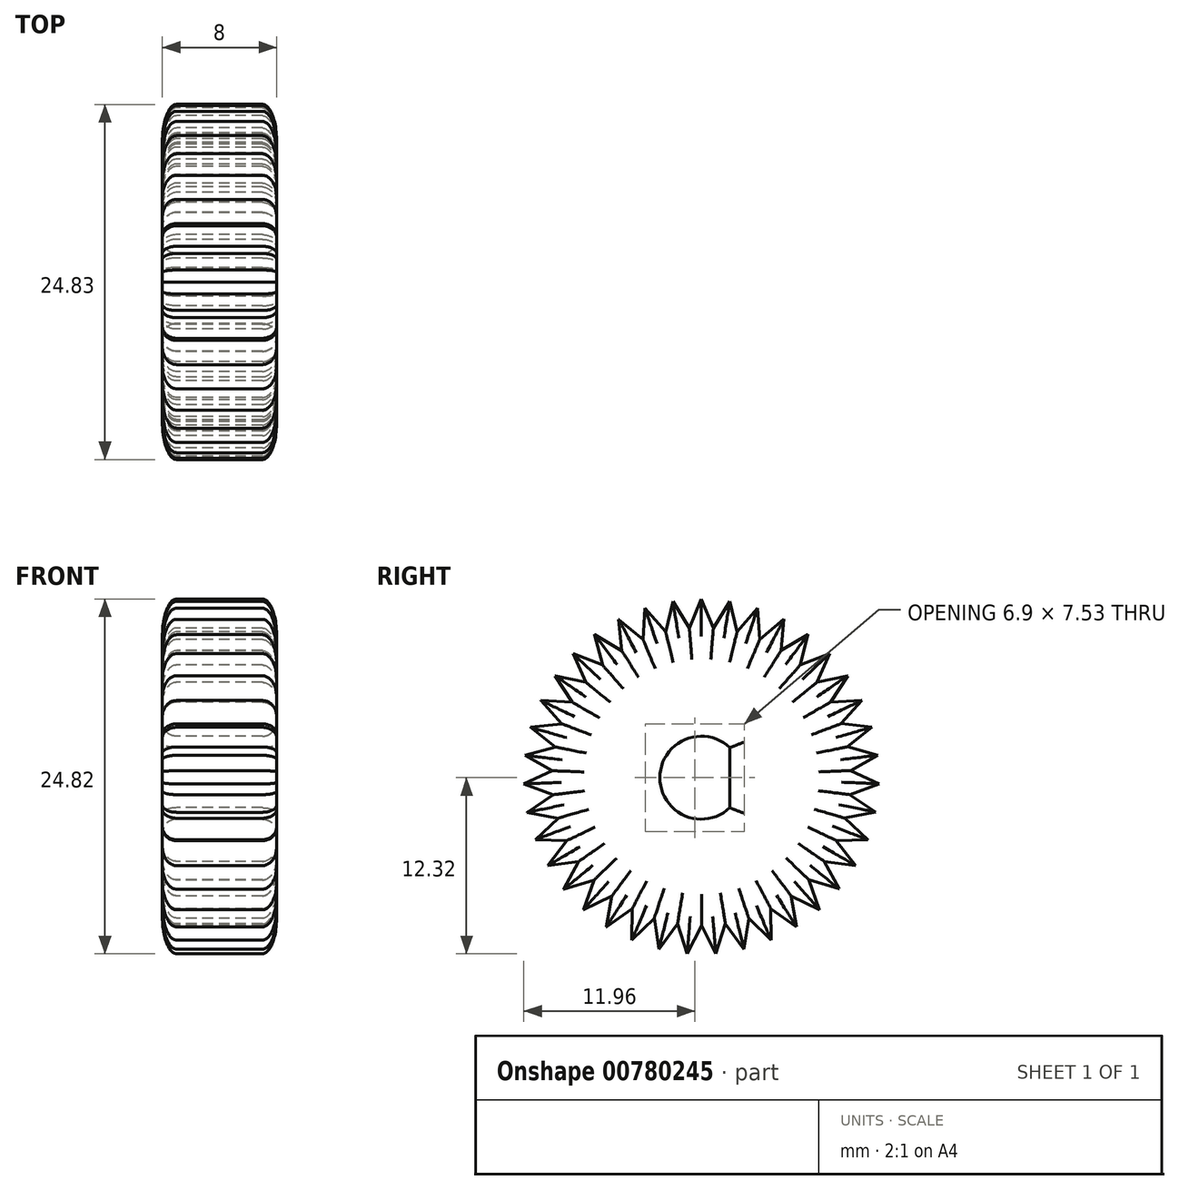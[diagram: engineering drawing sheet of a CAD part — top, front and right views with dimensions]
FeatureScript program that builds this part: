
annotation { "Feature Type Name" : "Feature", "Feature Type Description" : "" }
export const myFeature = defineFeature(function(context is Context, id is Id, definition is map)
    precondition{}
    {
        {
            var Q0;
            Q0=qCreatedBy(makeId("Right.planeOp"),FACE);
            var sketch = newSketch(context, id + "F0", { "sketchPlane" : qUnion([Q0])});
            skCircle(sketch, "E0", {"center": v(0, 0) * mm, "radius": 10.5 * mm, "construction": true});
            skCircle(sketch, "E1", {"center": v(0, 0) * mm, "radius": 2.9 * mm});
            skLineSegment(sketch, "E2", {"start": v(0, 0) * mm, "end": v(0, 12.5) * mm, "construction": true});
            skLineSegment(sketch, "E3", {"start": v(0, 12.5) * mm, "end": v(0.84, 10.47) * mm});
            skCircle(sketch, "E4", {"center": v(0, 0) * mm, "radius": 12.5 * mm, "construction": true});
            skLineSegment(sketch, "E5", {"start": v(0.84, 10.47) * mm, "end": v(2, 12.34) * mm});
            skLineSegment(sketch, "E6", {"start": v(2, 12.34) * mm, "end": v(0, 0) * mm, "construction": true});
            skLineSegment(sketch, "E7.1.0", {"start": v(-2, 12.34) * mm, "end": v(-0.84, 10.47) * mm});
            skLineSegment(sketch, "E7.1.1", {"start": v(-0.84, 10.47) * mm, "end": v(0, 12.5) * mm});
            skLineSegment(sketch, "E7.2.0", {"start": v(-3.94, 11.86) * mm, "end": v(-2.5, 10.2) * mm});
            skLineSegment(sketch, "E7.2.1", {"start": v(-2.5, 10.2) * mm, "end": v(-2, 12.34) * mm});
            skLineSegment(sketch, "E7.3.0", {"start": v(-5.77, 11.07) * mm, "end": v(-4.09, 9.66) * mm});
            skLineSegment(sketch, "E7.3.1", {"start": v(-4.09, 9.66) * mm, "end": v(-3.94, 11.86) * mm});
            skLineSegment(sketch, "E7.4.0", {"start": v(-7.46, 10) * mm, "end": v(-5.57, 8.88) * mm});
            skLineSegment(sketch, "E7.4.1", {"start": v(-5.57, 8.88) * mm, "end": v(-5.77, 11.07) * mm});
            skLineSegment(sketch, "E7.5.0", {"start": v(-8.96, 8.68) * mm, "end": v(-6.91, 7.87) * mm});
            skLineSegment(sketch, "E7.5.1", {"start": v(-6.91, 7.87) * mm, "end": v(-7.46, 10) * mm});
            skLineSegment(sketch, "E7.6.0", {"start": v(-10.23, 7.13) * mm, "end": v(-8.07, 6.66) * mm});
            skLineSegment(sketch, "E7.6.1", {"start": v(-8.07, 6.66) * mm, "end": v(-8.96, 8.68) * mm});
            skLineSegment(sketch, "E7.7.0", {"start": v(-11.22, 5.4) * mm, "end": v(-9.03, 5.28) * mm});
            skLineSegment(sketch, "E7.7.1", {"start": v(-9.03, 5.28) * mm, "end": v(-10.23, 7.13) * mm});
            skLineSegment(sketch, "E7.8.0", {"start": v(-11.93, 3.52) * mm, "end": v(-9.75, 3.77) * mm});
            skLineSegment(sketch, "E7.8.1", {"start": v(-9.75, 3.77) * mm, "end": v(-11.22, 5.4) * mm});
            skLineSegment(sketch, "E7.9.0", {"start": v(-12.33, 1.56) * mm, "end": v(-10.21, 2.15) * mm});
            skLineSegment(sketch, "E7.9.1", {"start": v(-10.21, 2.15) * mm, "end": v(-11.93, 3.52) * mm});
            skLineSegment(sketch, "E7.10.0", {"start": v(-12.41, -0.43) * mm, "end": v(-10.41, 0.49) * mm});
            skLineSegment(sketch, "E7.10.1", {"start": v(-10.41, 0.49) * mm, "end": v(-12.33, 1.56) * mm});
            skLineSegment(sketch, "E7.11.0", {"start": v(-12.17, -2.42) * mm, "end": v(-10.34, -1.19) * mm});
            skLineSegment(sketch, "E7.11.1", {"start": v(-10.34, -1.19) * mm, "end": v(-12.41, -0.43) * mm});
            skLineSegment(sketch, "E7.12.0", {"start": v(-11.61, -4.34) * mm, "end": v(-10, -2.83) * mm});
            skLineSegment(sketch, "E7.12.1", {"start": v(-10, -2.83) * mm, "end": v(-12.17, -2.42) * mm});
            skLineSegment(sketch, "E7.13.0", {"start": v(-10.75, -6.15) * mm, "end": v(-9.41, -4.4) * mm});
            skLineSegment(sketch, "E7.13.1", {"start": v(-9.41, -4.4) * mm, "end": v(-11.61, -4.34) * mm});
            skLineSegment(sketch, "E7.14.0", {"start": v(-9.62, -7.8) * mm, "end": v(-8.57, -5.85) * mm});
            skLineSegment(sketch, "E7.14.1", {"start": v(-8.57, -5.85) * mm, "end": v(-10.75, -6.15) * mm});
            skLineSegment(sketch, "E7.15.0", {"start": v(-8.23, -9.23) * mm, "end": v(-7.51, -7.15) * mm});
            skLineSegment(sketch, "E7.15.1", {"start": v(-7.51, -7.15) * mm, "end": v(-9.62, -7.8) * mm});
            skLineSegment(sketch, "E7.16.0", {"start": v(-6.63, -10.43) * mm, "end": v(-6.25, -8.27) * mm});
            skLineSegment(sketch, "E7.16.1", {"start": v(-6.25, -8.27) * mm, "end": v(-8.23, -9.23) * mm});
            skLineSegment(sketch, "E7.17.0", {"start": v(-4.86, -11.36) * mm, "end": v(-4.84, -9.16) * mm});
            skLineSegment(sketch, "E7.17.1", {"start": v(-4.84, -9.16) * mm, "end": v(-6.63, -10.43) * mm});
            skLineSegment(sketch, "E7.18.0", {"start": v(-2.96, -12) * mm, "end": v(-3.3, -9.82) * mm});
            skLineSegment(sketch, "E7.18.1", {"start": v(-3.3, -9.82) * mm, "end": v(-4.86, -11.36) * mm});
            skLineSegment(sketch, "E7.19.0", {"start": v(-0.99, -12.32) * mm, "end": v(-1.66, -10.22) * mm});
            skLineSegment(sketch, "E7.19.1", {"start": v(-1.66, -10.22) * mm, "end": v(-2.96, -12) * mm});
            skLineSegment(sketch, "E7.20.0", {"start": v(1.01, -12.31) * mm, "end": v(0.01, -10.35) * mm});
            skLineSegment(sketch, "E7.20.1", {"start": v(0.01, -10.35) * mm, "end": v(-0.99, -12.32) * mm});
            skLineSegment(sketch, "E7.21.0", {"start": v(2.99, -12) * mm, "end": v(1.68, -10.22) * mm});
            skLineSegment(sketch, "E7.21.1", {"start": v(1.68, -10.22) * mm, "end": v(1.01, -12.31) * mm});
            skLineSegment(sketch, "E7.22.0", {"start": v(4.88, -11.36) * mm, "end": v(3.31, -9.82) * mm});
            skLineSegment(sketch, "E7.22.1", {"start": v(3.31, -9.82) * mm, "end": v(2.99, -12) * mm});
            skLineSegment(sketch, "E7.23.0", {"start": v(6.65, -10.43) * mm, "end": v(4.86, -9.16) * mm});
            skLineSegment(sketch, "E7.23.1", {"start": v(4.86, -9.16) * mm, "end": v(4.88, -11.36) * mm});
            skLineSegment(sketch, "E7.24.0", {"start": v(8.25, -9.23) * mm, "end": v(6.27, -8.26) * mm});
            skLineSegment(sketch, "E7.24.1", {"start": v(6.27, -8.26) * mm, "end": v(6.65, -10.43) * mm});
            skLineSegment(sketch, "E7.25.0", {"start": v(9.64, -7.78) * mm, "end": v(7.53, -7.15) * mm});
            skLineSegment(sketch, "E7.25.1", {"start": v(7.53, -7.15) * mm, "end": v(8.25, -9.23) * mm});
            skLineSegment(sketch, "E7.26.0", {"start": v(10.77, -6.14) * mm, "end": v(8.6, -5.85) * mm});
            skLineSegment(sketch, "E7.26.1", {"start": v(8.6, -5.85) * mm, "end": v(9.64, -7.78) * mm});
            skLineSegment(sketch, "E7.27.0", {"start": v(11.63, -4.33) * mm, "end": v(9.43, -4.4) * mm});
            skLineSegment(sketch, "E7.27.1", {"start": v(9.43, -4.4) * mm, "end": v(10.77, -6.14) * mm});
            skLineSegment(sketch, "E7.28.0", {"start": v(12.18, -2.4) * mm, "end": v(10.02, -2.82) * mm});
            skLineSegment(sketch, "E7.28.1", {"start": v(10.02, -2.82) * mm, "end": v(11.63, -4.33) * mm});
            skLineSegment(sketch, "E7.29.0", {"start": v(12.42, -0.42) * mm, "end": v(10.36, -1.18) * mm});
            skLineSegment(sketch, "E7.29.1", {"start": v(10.36, -1.18) * mm, "end": v(12.18, -2.4) * mm});
            skLineSegment(sketch, "E7.30.0", {"start": v(12.34, 1.58) * mm, "end": v(10.42, 0.5) * mm});
            skLineSegment(sketch, "E7.30.1", {"start": v(10.42, 0.5) * mm, "end": v(12.42, -0.42) * mm});
            skLineSegment(sketch, "E7.31.0", {"start": v(11.94, 3.54) * mm, "end": v(10.22, 2.16) * mm});
            skLineSegment(sketch, "E7.31.1", {"start": v(10.22, 2.16) * mm, "end": v(12.34, 1.58) * mm});
            skLineSegment(sketch, "E7.32.0", {"start": v(11.23, 5.4) * mm, "end": v(9.75, 3.77) * mm});
            skLineSegment(sketch, "E7.32.1", {"start": v(9.75, 3.77) * mm, "end": v(11.94, 3.54) * mm});
            skLineSegment(sketch, "E7.33.0", {"start": v(10.23, 7.14) * mm, "end": v(9.03, 5.3) * mm});
            skLineSegment(sketch, "E7.33.1", {"start": v(9.03, 5.3) * mm, "end": v(11.23, 5.4) * mm});
            skLineSegment(sketch, "E7.34.0", {"start": v(8.96, 8.69) * mm, "end": v(8.08, 6.67) * mm});
            skLineSegment(sketch, "E7.34.1", {"start": v(8.08, 6.67) * mm, "end": v(10.23, 7.14) * mm});
            skLineSegment(sketch, "E7.35.0", {"start": v(7.47, 10.01) * mm, "end": v(6.92, 7.88) * mm});
            skLineSegment(sketch, "E7.35.1", {"start": v(6.92, 7.88) * mm, "end": v(8.96, 8.69) * mm});
            skLineSegment(sketch, "E7.36.0", {"start": v(5.78, 11.08) * mm, "end": v(5.57, 8.89) * mm});
            skLineSegment(sketch, "E7.36.1", {"start": v(5.57, 8.89) * mm, "end": v(7.47, 10.01) * mm});
            skLineSegment(sketch, "E7.37.0", {"start": v(3.94, 11.86) * mm, "end": v(4.09, 9.67) * mm});
            skLineSegment(sketch, "E7.37.1", {"start": v(4.09, 9.67) * mm, "end": v(5.78, 11.08) * mm});
            skLineSegment(sketch, "E7.38.0", {"start": v(2, 12.34) * mm, "end": v(2.5, 10.2) * mm});
            skLineSegment(sketch, "E7.38.1", {"start": v(2.5, 10.2) * mm, "end": v(3.94, 11.86) * mm});
            skPoint(sketch, "E7.center", {"position": v(0, 0.07) * mm});
            skSolve(sketch);
        }
        {
            var Q0;
            Q0=makeQuery(id+"F0.imprint","IMPRINT",FACE,{"disambiguationData":[TD([[makeQuery(id+"F0.imprint","IMPRINT",EDGE,{"derivedFrom":sQuery(id+"F0.wireOp",EDGE,"E1")}),-1.0]])]});
            extrude(context, id + "F1", {"entities" : qUnion([Q0]), "depth" : 8 * mm, "offsetDistance" : 25.4 * mm});
        }
        {
            var Q0;
            Q0=qCreatedBy(makeId("Right.planeOp"),FACE);
            var sketch = newSketch(context, id + "F2", { "sketchPlane" : qUnion([Q0])});
            skLineSegment(sketch, "E8", {"start": v(2, 2.1) * mm, "end": v(2, -2.1) * mm});
            skArc(sketch, "E9", {"start": v(2, -2.1) * mm, "mid": v(2.9, 0) * mm, "end": v(2, 2.1) * mm});
            skSolve(sketch);
        }
        {
            var Q0;
            Q0=qSketchRegion(id+"F2",true);
            extrude(context, id + "F3", {"entities" : qUnion([Q0]), "operationType" : NewBodyOperationType.ADD, "depth" : 8 * mm, "offsetDistance" : 25.4 * mm});
        }
        {
            var Q0;
            Q0=makeQuery(id+"F3.boolean.opBoolean","MERGE",FACE,{"derivedFrom":[makeQuery(id+"F1.opExtrude","CAP_FACE",FACE,{"disambiguationData":[OSD([sQuery(id+"F0.wireOp",EDGE,"E1"),sQuery(id+"F0.wireOp",EDGE,"E3"),sQuery(id+"F0.wireOp",EDGE,"E5"),sQuery(id+"F0.wireOp",EDGE,"E7.1.0"),sQuery(id+"F0.wireOp",EDGE,"E7.1.1"),sQuery(id+"F0.wireOp",EDGE,"E7.2.0"),sQuery(id+"F0.wireOp",EDGE,"E7.2.1"),sQuery(id+"F0.wireOp",EDGE,"E7.3.0"),sQuery(id+"F0.wireOp",EDGE,"E7.3.1"),sQuery(id+"F0.wireOp",EDGE,"E7.4.0"),sQuery(id+"F0.wireOp",EDGE,"E7.4.1"),sQuery(id+"F0.wireOp",EDGE,"E7.5.0"),sQuery(id+"F0.wireOp",EDGE,"E7.5.1"),sQuery(id+"F0.wireOp",EDGE,"E7.6.0"),sQuery(id+"F0.wireOp",EDGE,"E7.6.1"),sQuery(id+"F0.wireOp",EDGE,"E7.7.0"),sQuery(id+"F0.wireOp",EDGE,"E7.7.1"),sQuery(id+"F0.wireOp",EDGE,"E7.8.0"),sQuery(id+"F0.wireOp",EDGE,"E7.8.1"),sQuery(id+"F0.wireOp",EDGE,"E7.9.0"),sQuery(id+"F0.wireOp",EDGE,"E7.9.1"),sQuery(id+"F0.wireOp",EDGE,"E7.10.0"),sQuery(id+"F0.wireOp",EDGE,"E7.10.1"),sQuery(id+"F0.wireOp",EDGE,"E7.11.0"),sQuery(id+"F0.wireOp",EDGE,"E7.11.1"),sQuery(id+"F0.wireOp",EDGE,"E7.12.0"),sQuery(id+"F0.wireOp",EDGE,"E7.12.1"),sQuery(id+"F0.wireOp",EDGE,"E7.13.0"),sQuery(id+"F0.wireOp",EDGE,"E7.13.1"),sQuery(id+"F0.wireOp",EDGE,"E7.14.0"),sQuery(id+"F0.wireOp",EDGE,"E7.14.1"),sQuery(id+"F0.wireOp",EDGE,"E7.15.0"),sQuery(id+"F0.wireOp",EDGE,"E7.15.1"),sQuery(id+"F0.wireOp",EDGE,"E7.16.0"),sQuery(id+"F0.wireOp",EDGE,"E7.16.1"),sQuery(id+"F0.wireOp",EDGE,"E7.17.0"),sQuery(id+"F0.wireOp",EDGE,"E7.17.1"),sQuery(id+"F0.wireOp",EDGE,"E7.18.0"),sQuery(id+"F0.wireOp",EDGE,"E7.18.1"),sQuery(id+"F0.wireOp",EDGE,"E7.19.0"),sQuery(id+"F0.wireOp",EDGE,"E7.19.1"),sQuery(id+"F0.wireOp",EDGE,"E7.20.0"),sQuery(id+"F0.wireOp",EDGE,"E7.20.1"),sQuery(id+"F0.wireOp",EDGE,"E7.21.0"),sQuery(id+"F0.wireOp",EDGE,"E7.21.1"),sQuery(id+"F0.wireOp",EDGE,"E7.22.0"),sQuery(id+"F0.wireOp",EDGE,"E7.22.1"),sQuery(id+"F0.wireOp",EDGE,"E7.23.0"),sQuery(id+"F0.wireOp",EDGE,"E7.23.1"),sQuery(id+"F0.wireOp",EDGE,"E7.24.0"),sQuery(id+"F0.wireOp",EDGE,"E7.24.1"),sQuery(id+"F0.wireOp",EDGE,"E7.25.0"),sQuery(id+"F0.wireOp",EDGE,"E7.25.1"),sQuery(id+"F0.wireOp",EDGE,"E7.26.0"),sQuery(id+"F0.wireOp",EDGE,"E7.26.1"),sQuery(id+"F0.wireOp",EDGE,"E7.27.0"),sQuery(id+"F0.wireOp",EDGE,"E7.27.1"),sQuery(id+"F0.wireOp",EDGE,"E7.28.0"),sQuery(id+"F0.wireOp",EDGE,"E7.28.1"),sQuery(id+"F0.wireOp",EDGE,"E7.29.0"),sQuery(id+"F0.wireOp",EDGE,"E7.29.1"),sQuery(id+"F0.wireOp",EDGE,"E7.30.0"),sQuery(id+"F0.wireOp",EDGE,"E7.30.1"),sQuery(id+"F0.wireOp",EDGE,"E7.31.0"),sQuery(id+"F0.wireOp",EDGE,"E7.31.1"),sQuery(id+"F0.wireOp",EDGE,"E7.32.0"),sQuery(id+"F0.wireOp",EDGE,"E7.32.1"),sQuery(id+"F0.wireOp",EDGE,"E7.33.0"),sQuery(id+"F0.wireOp",EDGE,"E7.33.1"),sQuery(id+"F0.wireOp",EDGE,"E7.34.0"),sQuery(id+"F0.wireOp",EDGE,"E7.34.1"),sQuery(id+"F0.wireOp",EDGE,"E7.35.0"),sQuery(id+"F0.wireOp",EDGE,"E7.35.1"),sQuery(id+"F0.wireOp",EDGE,"E7.36.0"),sQuery(id+"F0.wireOp",EDGE,"E7.36.1"),sQuery(id+"F0.wireOp",EDGE,"E7.37.0"),sQuery(id+"F0.wireOp",EDGE,"E7.37.1"),sQuery(id+"F0.wireOp",EDGE,"E7.38.0"),sQuery(id+"F0.wireOp",EDGE,"E7.38.1")])],"isStart":false}),makeQuery(id+"F3.opExtrude","CAP_FACE",FACE,{"disambiguationData":[OSD([sQuery(id+"F2.wireOp",EDGE,"E8"),sQuery(id+"F2.wireOp",EDGE,"E9")])],"isStart":false})]});
            fillet(context, id + "F4", {"entities" : qUnion([Q0]), "radius" : 1 * mm, "tangentPropagation" : true, "allowEdgeOverflow" : false});
        }
        {
            var Q0;
            Q0=makeQuery(id+"F3.boolean.opBoolean","MERGE",FACE,{"derivedFrom":[makeQuery(id+"F1.opExtrude","CAP_FACE",FACE,{"disambiguationData":[OSD([sQuery(id+"F0.wireOp",EDGE,"E1"),sQuery(id+"F0.wireOp",EDGE,"E3"),sQuery(id+"F0.wireOp",EDGE,"E5"),sQuery(id+"F0.wireOp",EDGE,"E7.1.0"),sQuery(id+"F0.wireOp",EDGE,"E7.1.1"),sQuery(id+"F0.wireOp",EDGE,"E7.2.0"),sQuery(id+"F0.wireOp",EDGE,"E7.2.1"),sQuery(id+"F0.wireOp",EDGE,"E7.3.0"),sQuery(id+"F0.wireOp",EDGE,"E7.3.1"),sQuery(id+"F0.wireOp",EDGE,"E7.4.0"),sQuery(id+"F0.wireOp",EDGE,"E7.4.1"),sQuery(id+"F0.wireOp",EDGE,"E7.5.0"),sQuery(id+"F0.wireOp",EDGE,"E7.5.1"),sQuery(id+"F0.wireOp",EDGE,"E7.6.0"),sQuery(id+"F0.wireOp",EDGE,"E7.6.1"),sQuery(id+"F0.wireOp",EDGE,"E7.7.0"),sQuery(id+"F0.wireOp",EDGE,"E7.7.1"),sQuery(id+"F0.wireOp",EDGE,"E7.8.0"),sQuery(id+"F0.wireOp",EDGE,"E7.8.1"),sQuery(id+"F0.wireOp",EDGE,"E7.9.0"),sQuery(id+"F0.wireOp",EDGE,"E7.9.1"),sQuery(id+"F0.wireOp",EDGE,"E7.10.0"),sQuery(id+"F0.wireOp",EDGE,"E7.10.1"),sQuery(id+"F0.wireOp",EDGE,"E7.11.0"),sQuery(id+"F0.wireOp",EDGE,"E7.11.1"),sQuery(id+"F0.wireOp",EDGE,"E7.12.0"),sQuery(id+"F0.wireOp",EDGE,"E7.12.1"),sQuery(id+"F0.wireOp",EDGE,"E7.13.0"),sQuery(id+"F0.wireOp",EDGE,"E7.13.1"),sQuery(id+"F0.wireOp",EDGE,"E7.14.0"),sQuery(id+"F0.wireOp",EDGE,"E7.14.1"),sQuery(id+"F0.wireOp",EDGE,"E7.15.0"),sQuery(id+"F0.wireOp",EDGE,"E7.15.1"),sQuery(id+"F0.wireOp",EDGE,"E7.16.0"),sQuery(id+"F0.wireOp",EDGE,"E7.16.1"),sQuery(id+"F0.wireOp",EDGE,"E7.17.0"),sQuery(id+"F0.wireOp",EDGE,"E7.17.1"),sQuery(id+"F0.wireOp",EDGE,"E7.18.0"),sQuery(id+"F0.wireOp",EDGE,"E7.18.1"),sQuery(id+"F0.wireOp",EDGE,"E7.19.0"),sQuery(id+"F0.wireOp",EDGE,"E7.19.1"),sQuery(id+"F0.wireOp",EDGE,"E7.20.0"),sQuery(id+"F0.wireOp",EDGE,"E7.20.1"),sQuery(id+"F0.wireOp",EDGE,"E7.21.0"),sQuery(id+"F0.wireOp",EDGE,"E7.21.1"),sQuery(id+"F0.wireOp",EDGE,"E7.22.0"),sQuery(id+"F0.wireOp",EDGE,"E7.22.1"),sQuery(id+"F0.wireOp",EDGE,"E7.23.0"),sQuery(id+"F0.wireOp",EDGE,"E7.23.1"),sQuery(id+"F0.wireOp",EDGE,"E7.24.0"),sQuery(id+"F0.wireOp",EDGE,"E7.24.1"),sQuery(id+"F0.wireOp",EDGE,"E7.25.0"),sQuery(id+"F0.wireOp",EDGE,"E7.25.1"),sQuery(id+"F0.wireOp",EDGE,"E7.26.0"),sQuery(id+"F0.wireOp",EDGE,"E7.26.1"),sQuery(id+"F0.wireOp",EDGE,"E7.27.0"),sQuery(id+"F0.wireOp",EDGE,"E7.27.1"),sQuery(id+"F0.wireOp",EDGE,"E7.28.0"),sQuery(id+"F0.wireOp",EDGE,"E7.28.1"),sQuery(id+"F0.wireOp",EDGE,"E7.29.0"),sQuery(id+"F0.wireOp",EDGE,"E7.29.1"),sQuery(id+"F0.wireOp",EDGE,"E7.30.0"),sQuery(id+"F0.wireOp",EDGE,"E7.30.1"),sQuery(id+"F0.wireOp",EDGE,"E7.31.0"),sQuery(id+"F0.wireOp",EDGE,"E7.31.1"),sQuery(id+"F0.wireOp",EDGE,"E7.32.0"),sQuery(id+"F0.wireOp",EDGE,"E7.32.1"),sQuery(id+"F0.wireOp",EDGE,"E7.33.0"),sQuery(id+"F0.wireOp",EDGE,"E7.33.1"),sQuery(id+"F0.wireOp",EDGE,"E7.34.0"),sQuery(id+"F0.wireOp",EDGE,"E7.34.1"),sQuery(id+"F0.wireOp",EDGE,"E7.35.0"),sQuery(id+"F0.wireOp",EDGE,"E7.35.1"),sQuery(id+"F0.wireOp",EDGE,"E7.36.0"),sQuery(id+"F0.wireOp",EDGE,"E7.36.1"),sQuery(id+"F0.wireOp",EDGE,"E7.37.0"),sQuery(id+"F0.wireOp",EDGE,"E7.37.1"),sQuery(id+"F0.wireOp",EDGE,"E7.38.0"),sQuery(id+"F0.wireOp",EDGE,"E7.38.1")])],"isStart":true}),makeQuery(id+"F3.opExtrude","CAP_FACE",FACE,{"disambiguationData":[OSD([sQuery(id+"F2.wireOp",EDGE,"E8"),sQuery(id+"F2.wireOp",EDGE,"E9")])],"isStart":true})]});
            fillet(context, id + "F5", {"entities" : qUnion([Q0]), "radius" : 1 * mm, "tangentPropagation" : true, "allowEdgeOverflow" : false});
        }
    });
